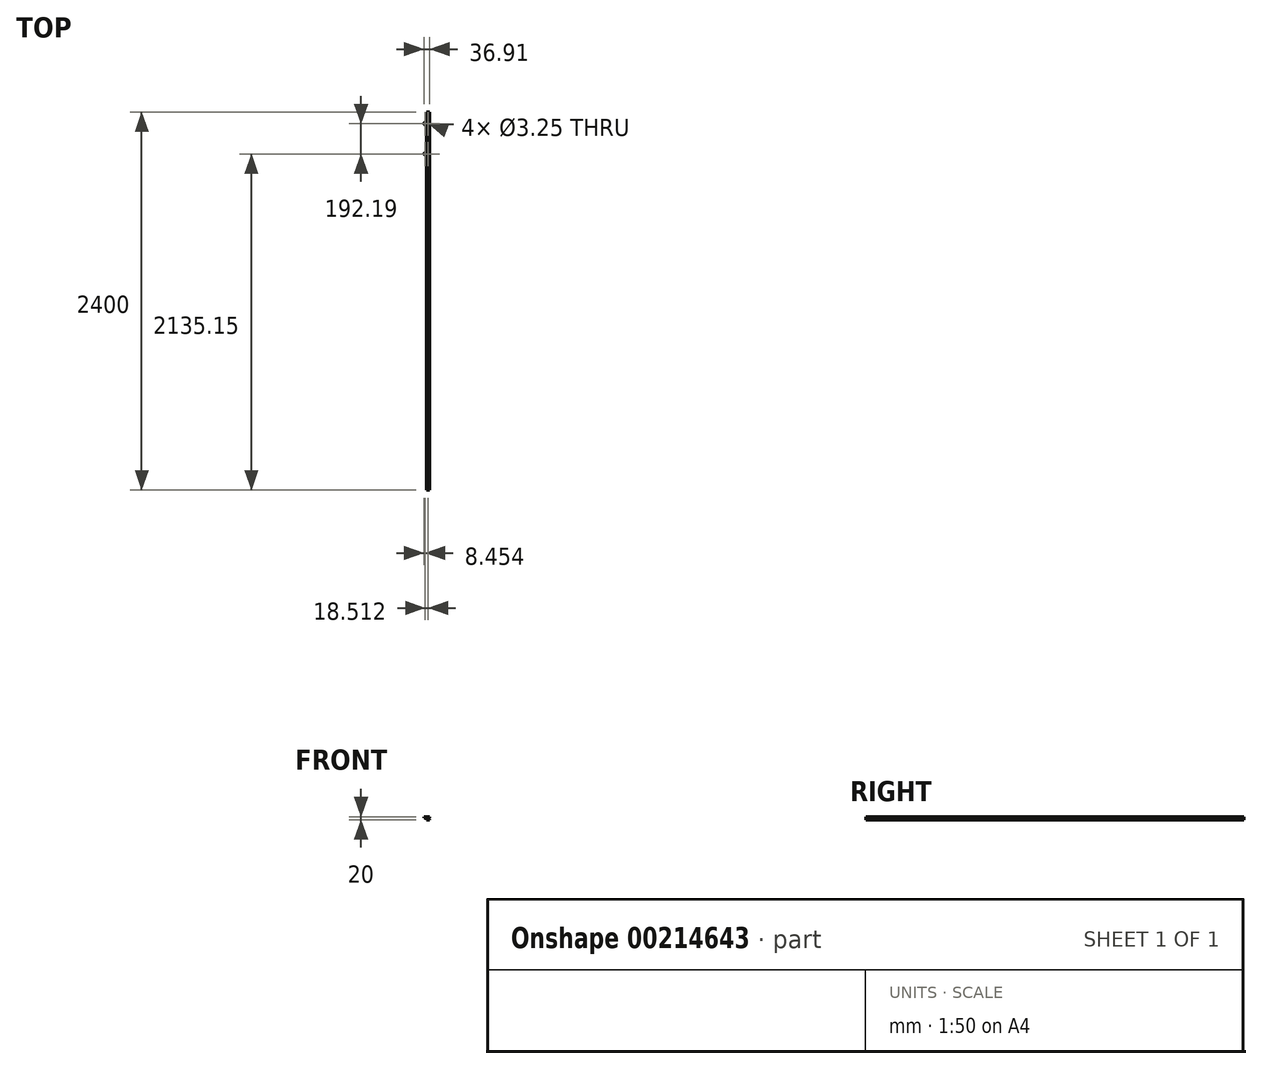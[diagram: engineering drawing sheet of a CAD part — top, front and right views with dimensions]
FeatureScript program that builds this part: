
annotation { "Feature Type Name" : "Feature", "Feature Type Description" : "" }
export const myFeature = defineFeature(function(context is Context, id is Id, definition is map)
    precondition{}
    {
        {
            var Q0;
            Q0=qCreatedBy(makeId("Front.planeOp"),FACE);
            var sketch = newSketch(context, id + "F0", { "sketchPlane" : qUnion([Q0])});
            skLineSegment(sketch, "E0", {"start": v(0, 0) * mm, "end": v(20, 0) * mm});
            skLineSegment(sketch, "E1", {"start": v(20, 0) * mm, "end": v(20, 1.6) * mm});
            skLineSegment(sketch, "E2", {"start": v(0, 0) * mm, "end": v(0, 20) * mm});
            skLineSegment(sketch, "E3", {"start": v(0, 20) * mm, "end": v(1.6, 20) * mm});
            skLineSegment(sketch, "E4", {"start": v(1.6, 20) * mm, "end": v(1.6, 1.6) * mm});
            skLineSegment(sketch, "E5", {"start": v(1.6, 1.6) * mm, "end": v(20, 1.6) * mm});
            skSolve(sketch);
        }
        {
            var Q0;
            Q0 = qSketchRegion(id + "F0", true);
            extrude(context, id + "F1", {"entities" : qUnion([Q0]), "depth" : 2400 * mm});
        }
        {
            var Q0;
            Q0=makeQuery(id+"F1.opExtrude","SWEPT_FACE",FACE,{"disambiguationData":[OSD([sQuery(id+"F0.wireOp",EDGE,"E3")])]});
            var sketch = newSketch(context, id + "F2", { "sketchPlane" : qUnion([Q0])});
            skLineSegment(sketch, "E6.bottom", {"start": v(10.06, -264.85) * mm, "end": v(-8.46, -264.85) * mm, "construction": true});
            skLineSegment(sketch, "E6.top", {"start": v(10.06, -72.66) * mm, "end": v(-8.46, -72.66) * mm, "construction": true});
            skLineSegment(sketch, "E6.left", {"start": v(10.06, -264.85) * mm, "end": v(10.06, -72.66) * mm, "construction": true});
            skLineSegment(sketch, "E6.right", {"start": v(-8.46, -264.85) * mm, "end": v(-8.46, -72.66) * mm, "construction": true});
            skLineSegment(sketch, "E7.0.0", {"start": v(1.6, 0) * mm, "end": v(0, 0) * mm, "construction": true});
            skLineSegment(sketch, "E7.0.1", {"start": v(0, 0) * mm, "end": v(0, -2400) * mm, "construction": true});
            skLineSegment(sketch, "E7.0.2", {"start": v(0, -2400) * mm, "end": v(1.6, -2400) * mm, "construction": true});
            skLineSegment(sketch, "E7.0.3", {"start": v(1.6, -2400) * mm, "end": v(1.6, 0) * mm, "construction": true});
            skLineSegment(sketch, "E8", {"start": v(0.8, -264.85) * mm, "end": v(0.8, -72.66) * mm, "construction": true});
            skCircle(sketch, "E9", {"center": v(-8.46, -264.85) * mm, "radius": 8.46 * mm});
            skCircle(sketch, "E10", {"center": v(10.06, -264.85) * mm, "radius": 8.46 * mm});
            skCircle(sketch, "E11", {"center": v(-8.46, -72.66) * mm, "radius": 8.46 * mm});
            skCircle(sketch, "E12", {"center": v(10.06, -72.66) * mm, "radius": 8.46 * mm});
            skCircle(sketch, "E13", {"center": v(-8.46, -264.85) * mm, "radius": 1.63 * mm});
            skCircle(sketch, "E14", {"center": v(10.06, -264.85) * mm, "radius": 1.63 * mm});
            skCircle(sketch, "E15", {"center": v(10.06, -72.66) * mm, "radius": 1.63 * mm});
            skCircle(sketch, "E16", {"center": v(-8.46, -72.66) * mm, "radius": 1.63 * mm});
            skSolve(sketch);
        }
        {
            var Q0;
            Q0 = qSketchRegion(id + "F2", true);
            extrude(context, id + "F3", {"entities" : qUnion([Q0]), "oppositeDirection" : true, "depth" : 8 * mm});
        }
    });
